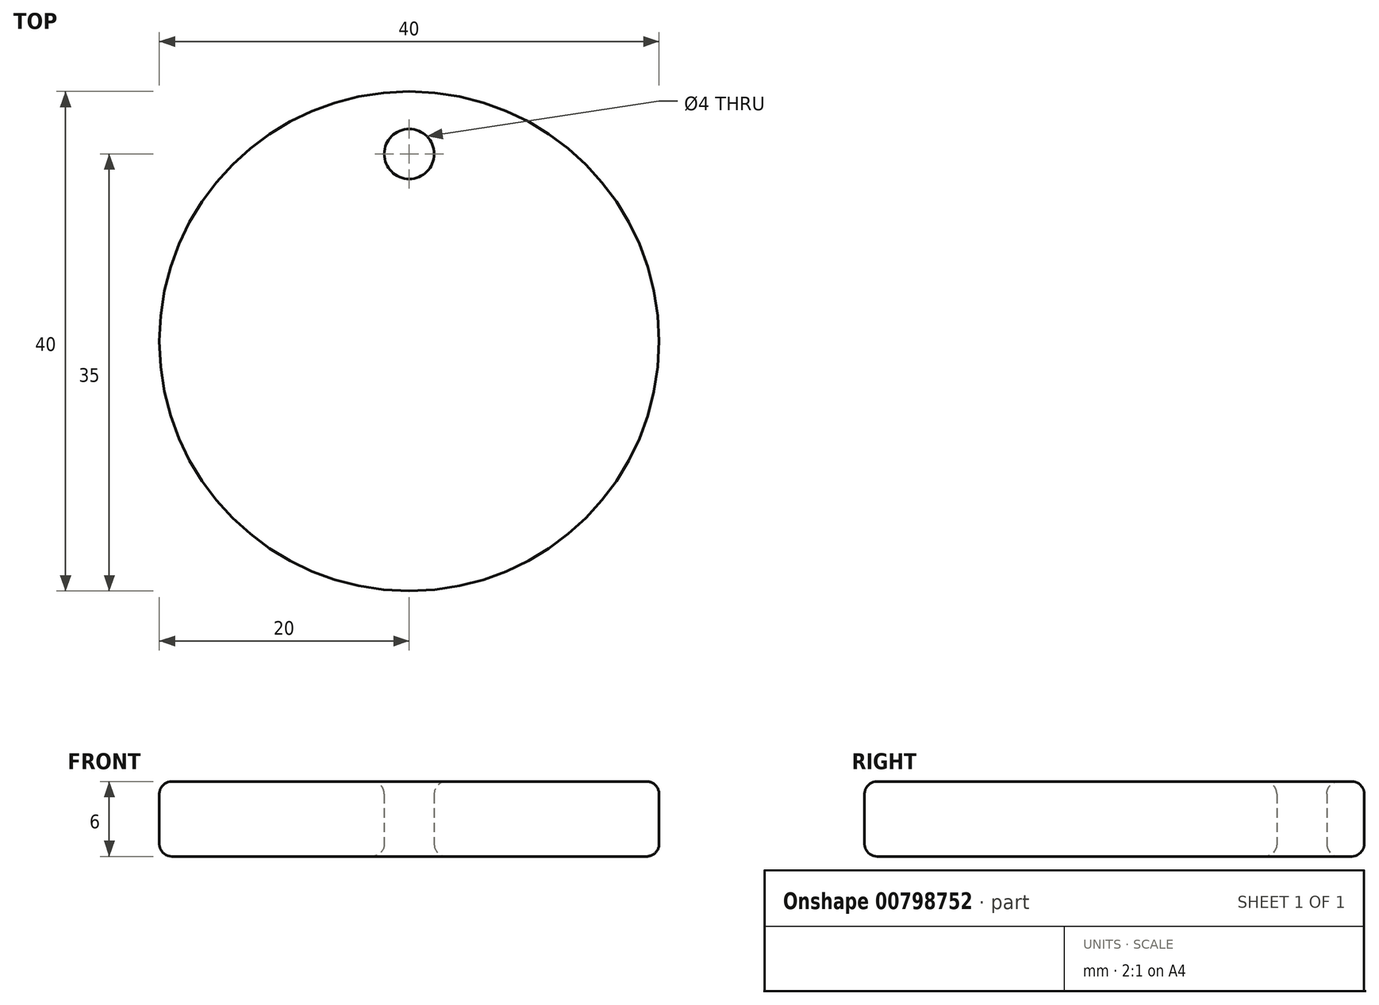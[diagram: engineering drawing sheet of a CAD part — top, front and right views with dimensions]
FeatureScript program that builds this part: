
annotation { "Feature Type Name" : "Feature", "Feature Type Description" : "" }
export const myFeature = defineFeature(function(context is Context, id is Id, definition is map)
    precondition{}
    {
        {
            var Q0;
            Q0=qCreatedBy(makeId("Top.planeOp"),FACE);
            var sketch = newSketch(context, id + "F0", { "sketchPlane" : qUnion([Q0])});
            skCircle(sketch, "E0", {"center": v(0, 0) * mm, "radius": 2 * mm});
            skCircle(sketch, "E1", {"center": v(0, -15) * mm, "radius": 20 * mm});
            skSolve(sketch);
        }
        {
            var Q0;
            Q0=qSketchRegion(id+"F0",true);
            extrude(context, id + "F1", {"entities" : qUnion([Q0]), "depth" : 6 * mm, "offsetDistance" : 25 * mm});
        }
        {
            var Q0;
            Q0=makeQuery(id+"F1.opExtrude","CAP_FACE",FACE,{"disambiguationData":[OSD([sQuery(id+"F0.wireOp",EDGE,"E0"),sQuery(id+"F0.wireOp",EDGE,"E1")])],"isStart":false});
            var Q1;
            Q1=makeQuery(id+"F1.opExtrude","CAP_FACE",FACE,{"disambiguationData":[OSD([sQuery(id+"F0.wireOp",EDGE,"E0"),sQuery(id+"F0.wireOp",EDGE,"E1")])],"isStart":true});
            fillet(context, id + "F2", {"entities" : qUnion([Q0, Q1]), "radius" : 1 * mm, "tangentPropagation" : true, "allowEdgeOverflow" : false});
        }
    });
